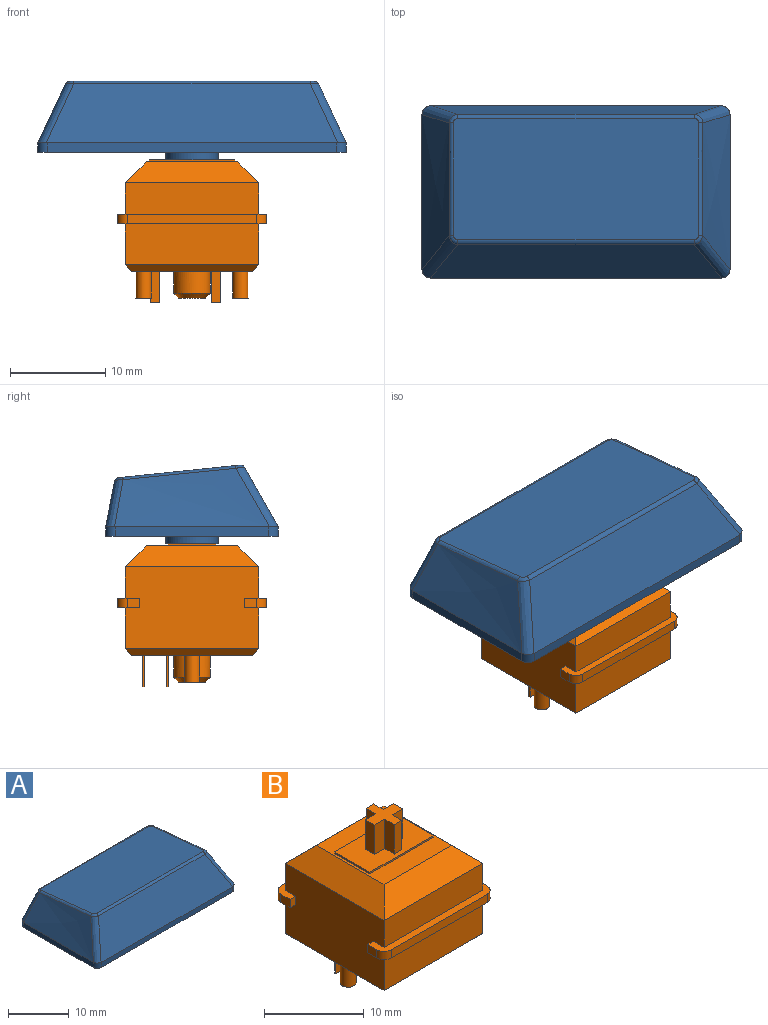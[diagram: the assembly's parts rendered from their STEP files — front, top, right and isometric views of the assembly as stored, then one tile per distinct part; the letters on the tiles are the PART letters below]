
ASSEMBLY  parts=2 mates=1
PART A: 50 faces, bbox 35.5x21.6x10.6 mm
  f0: plane 32.35x18.1mm, normal (0,0,-1), area 96mm2, adj f1,f2,f3,f4,f10,f12,f14,f16
  f1: plane 30.35x1mm, normal (0,-1,0), area 30.3mm2, adj f0,f8,f10,f12
  f2: plane 16.1x1mm, normal (1,0,0), area 16.1mm2, adj f0,f9,f10,f16
  f3: plane 30.35x1mm, normal (0,1,0), area 30.3mm2, adj f0,f6,f14,f15,f16,f17
  f4: plane 16.1x1mm, normal (-1,0,0), area 16.1mm2, adj f0,f7,f12,f14
  f5: plane 25.78x12.74mm, normal (0,0.1,0.99), area 329.4mm2, adj f18,f19,f20,f21,f22,f23,f24,f25
  f6: plane 30.26x4.75mm, normal (0,0.98,0.19), area 133.2mm2, adj f3,f15,f17,f20
  f7: bspline ~18.1x6.51mm, area 88.3mm2, adj f4,f12,f13,f14,f15,f19
  f8: plane 30.6x6.23mm, normal (0,-0.87,0.49), area 198.3mm2, adj f1,f10,f11,f12,f13,f23
  f9: bspline ~18.1x6.51mm, area 88.3mm2, adj f2,f10,f11,f16,f17,f24
  f10: cylinder r=1mm len=1.08mm, axis (0,0,1), area 1.7mm2, adj f0,f1,f2,f8,f9,f11
  f11: bspline ~8x5.25mm, area 10.6mm2, adj f8,f9,f10,f25
  f12: cylinder r=1mm len=1.08mm, axis (0,0,-1), area 1.7mm2, adj f0,f1,f4,f7,f8,f13
  f13: bspline ~8.02x5.26mm, area 10.6mm2, adj f7,f8,f12,f21
  f14: cylinder r=1mm len=1.01mm, axis (0,0,1), area 1.6mm2, adj f0,f3,f4,f7,f15
  f15: bspline ~7.53x4.96mm, area 8.3mm2, adj f3,f6,f7,f14,f18
  f16: cylinder r=1mm len=1.01mm, axis (0,0,-1), area 1.6mm2, adj f0,f2,f3,f9,f17
  f17: bspline ~7.51x4.95mm, area 8.3mm2, adj f3,f6,f9,f16,f22
  f18: bspline ~1.23x0.97mm, area 0.6mm2, adj f5,f15,f19,f20
  f19: bspline ~17.25x2.02mm, area 6.5mm2, adj f5,f7,f18,f21
  f20: cylinder r=0.5mm len=24.79mm, axis (-1,0,0), area 15.8mm2, adj f5,f6,f18,f22
  f21: bspline ~1.16x0.98mm, area 0.6mm2, adj f5,f13,f19,f23
  f22: bspline ~1.23x1.14mm, area 0.6mm2, adj f5,f17,f20,f24
  f23: cylinder r=0.5mm len=24.78mm, axis (-1,0,0), area 14.4mm2, adj f5,f8,f21,f25
  f24: bspline ~17.24x2.02mm, area 6.5mm2, adj f5,f9,f22,f25
  f25: bspline ~1.16x1mm, area 0.6mm2, adj f5,f11,f23,f24
  f26: plane 30.35x0.74mm, normal (0,1,0), area 22.3mm2, adj f0,f27,f29,f33
  f27: plane 16.13x0.81mm, normal (-1,0,0), area 12.2mm2, adj f0,f26,f28,f33,f34
  f28: plane 30.35x0.91mm, normal (0,-1,0), area 27.5mm2, adj f0,f27,f29,f31,f32,f34
  f29: plane 16.13x0.81mm, normal (1,0,0), area 12.2mm2, adj f0,f26,f28,f32,f33
  f30: plane 26.35x13.18mm, normal (0,-0.1,-0.99), area 280.3mm2, adj f31,f32,f33,f34,f45
  f31: plane 30.17x4.31mm, normal (0,-0.98,-0.19), area 121mm2, adj f28,f30,f32,f34
  f32: offset ~20.1x8.51mm, area 80.9mm2, adj f28,f29,f30,f31,f33
  f33: plane 30.38x5.75mm, normal (0,0.87,-0.49), area 182.1mm2, adj f26,f27,f29,f30,f32,f34
  f34: offset ~20.1x8.51mm, area 80.9mm2, adj f27,f28,f30,f31,f33
  f35: plane 6.68x1.35mm, normal (-1,0,0), area 8.9mm2, adj f36,f44,f47,f49
  f36: plane 6.68x1.5mm, normal (0,-1,0), area 10mm2, adj f35,f37,f44,f49
  f37: plane 6.82x1.3mm, normal (-1,0,0), area 8.8mm2, adj f36,f38,f44,f49
  f38: plane 6.82x1.5mm, normal (0,1,0), area 10.2mm2, adj f37,f39,f44,f49
  f39: plane 6.96x1.35mm, normal (-1,0,0), area 9.3mm2, adj f38,f40,f44,f49
  f40: plane 6.96x1mm, normal (0,1,0), area 7mm2, adj f39,f41,f44,f49
  f41: plane 6.96x1.35mm, normal (1,0,0), area 9.3mm2, adj f40,f42,f44,f49
  f42: plane 6.82x1.5mm, normal (0,1,0), area 10.2mm2, adj f41,f43,f44,f49
  f43: plane 6.82x1.3mm, normal (1,0,0), area 8.8mm2, adj f42,f44,f46,f49
  f44: plane 5.5x5.5mm, normal (0,0,-1), area 15.9mm2, adj f35,f36,f37,f38,f39,f40,f41,f42
  f45: cylinder r=2.75mm len=6.47mm, axis (0,0,-1), area 111.7mm2, adj f30,f44
  f46: plane 6.68x1.5mm, normal (0,-1,0), area 10mm2, adj f43,f44,f48,f49
  f47: plane 6.54x1mm, normal (0,-1,0), area 6.5mm2, adj f35,f44,f48,f49
  f48: plane 6.68x1.35mm, normal (1,0,0), area 8.9mm2, adj f44,f46,f47,f49
  f49: plane 4x4mm, normal (0,-0.1,-0.99), area 7.9mm2, adj f35,f36,f37,f38,f39,f40,f41,f42
PART B: 69 faces, bbox 15.6x15.6x18.6 mm
  f0: plane 15.6x2.3mm, normal (0,0,-1), area 14.4mm2, adj f2,f3,f28,f30,f35,f60,f62,f63
  f1: plane 15.6x2.3mm, normal (0,0,-1), area 14.4mm2, adj f28,f30,f33,f34,f36,f59,f61,f64
  f2: plane 1.3x1mm, normal (1,0,0), area 1.3mm2, adj f0,f32,f62,f66
  f3: plane 1.3x1mm, normal (-1,0,0), area 1.3mm2, adj f0,f32,f63,f68
  f4: plane 15.6x2.3mm, normal (0,0,1), area 14.4mm2, adj f28,f30,f31,f33,f34,f36,f61,f64
  f5: plane 14x2.2mm, normal (-0.71,0,0.71), area 36.7mm2, adj f6,f7,f26,f30
  f6: plane 14x2.2mm, normal (0,-0.71,0.71), area 36.7mm2, adj f5,f7,f27,f31
  f7: plane 9.6x9.6mm, normal (0,0,1), area 47.2mm2, adj f5,f6,f8,f9,f10,f11,f26,f27
  f8: plane 5x0.2mm, normal (1,0,0), area 1mm2, adj f7,f9,f11,f12
  f9: plane 9x0.2mm, normal (0,1,0), area 1.8mm2, adj f7,f8,f10,f12
  f10: plane 5x0.2mm, normal (-1,0,0), area 1mm2, adj f7,f9,f11,f12
  f11: plane 9x0.2mm, normal (0,-1,0), area 1.8mm2, adj f7,f8,f10,f12
  f12: plane 9x5mm, normal (0,0,1), area 36.9mm2, adj f8,f9,f10,f11,f13,f14,f15,f16
  f13: plane 3.6x1.35mm, normal (1,0,0), area 4.9mm2, adj f12,f14,f24,f25
  f14: plane 3.6x1.08mm, normal (0,1,0), area 3.9mm2, adj f12,f13,f15,f25
  f15: plane 3.6x1.35mm, normal (-1,0,0), area 4.9mm2, adj f12,f14,f16,f25
  f16: plane 3.6x1.46mm, normal (0,1,0), area 5.3mm2, adj f12,f15,f17,f25
  f17: plane 3.6x1.3mm, normal (-1,0,0), area 4.7mm2, adj f12,f16,f18,f25
  f18: plane 3.6x1.46mm, normal (0,-1,0), area 5.3mm2, adj f12,f17,f19,f25
  f19: plane 3.6x1.35mm, normal (-1,0,0), area 4.9mm2, adj f12,f18,f20,f25
  f20: plane 3.6x1.08mm, normal (0,-1,0), area 3.9mm2, adj f12,f19,f21,f25
  f21: plane 3.6x1.35mm, normal (1,0,0), area 4.9mm2, adj f12,f20,f22,f25
  f22: plane 3.6x1.46mm, normal (0,-1,0), area 5.3mm2, adj f12,f21,f23,f25
  f23: plane 3.6x1.3mm, normal (1,0,0), area 4.7mm2, adj f12,f22,f24,f25
  f24: plane 3.6x1.46mm, normal (0,1,0), area 5.3mm2, adj f12,f13,f23,f25
  f25: plane 4x4mm, normal (0,0,1), area 8.1mm2, adj f13,f14,f15,f16,f17,f18,f19,f20
  f26: plane 14x2.2mm, normal (0,0.71,0.71), area 36.7mm2, adj f5,f7,f27,f29
  f27: plane 14x2.2mm, normal (0.71,0,0.71), area 36.7mm2, adj f6,f7,f26,f28
  f28: plane 14x8.6mm, normal (1,0,0), area 117.4mm2, adj f0,f1,f4,f27,f29,f31,f32,f55
  f29: plane 14x3.3mm, normal (0,1,0), area 46.2mm2, adj f26,f28,f30,f32
  f30: plane 14x8.6mm, normal (-1,0,0), area 117.4mm2, adj f0,f1,f4,f5,f29,f31,f32,f57
  f31: plane 14x3.3mm, normal (0,-1,0), area 46.2mm2, adj f4,f6,f28,f30
  f32: plane 15.6x2.3mm, normal (0,0,1), area 14.4mm2, adj f2,f3,f28,f29,f30,f35,f62,f63
  f33: plane 13.6x1mm, normal (0,-1,0), area 13.6mm2, adj f1,f4,f61,f64
  f34: plane 1.3x1mm, normal (1,0,0), area 1.3mm2, adj f1,f4,f61,f65
  f35: plane 13.6x1mm, normal (0,1,0), area 13.6mm2, adj f0,f32,f62,f63
  f36: plane 1.3x1mm, normal (-1,0,0), area 1.3mm2, adj f1,f4,f64,f67
  f37: plane 2.85x2.85mm, normal (0,0,-1), area 6.4mm2, adj f38
  f38: cone r=1.43mm half-angle=45deg, axis (0,0,1), area 7.4mm2, adj f37,f43
  f39: plane 1x0.2mm, normal (0,0,-1), area 0.2mm2, adj f44,f45,f46,f47
  f40: plane 1x0.2mm, normal (0,0,-1), area 0.2mm2, adj f48,f49,f50,f51
  f41: plane 1.6x1.6mm, normal (0,0,-1), area 2mm2, adj f52
  f42: plane 1.6x1.6mm, normal (0,0,-1), area 2mm2, adj f53
  f43: cylinder r=1.93mm len=3.85mm, axis (0,0,1), area 27.8mm2, adj f38,f54
  f44: plane 3.3x0.2mm, normal (-1,0,0), area 0.7mm2, adj f39,f45,f47,f54
  f45: plane 3.3x1mm, normal (0,1,0), area 3.3mm2, adj f39,f44,f46,f54
  f46: plane 3.3x0.2mm, normal (1,0,0), area 0.7mm2, adj f39,f45,f47,f54
  f47: plane 3.3x1mm, normal (0,-1,0), area 3.3mm2, adj f39,f44,f46,f54
  f48: plane 3.3x0.2mm, normal (-1,0,0), area 0.7mm2, adj f40,f49,f51,f54
  f49: plane 3.3x1mm, normal (0,1,0), area 3.3mm2, adj f40,f48,f50,f54
  f50: plane 3.3x0.2mm, normal (1,0,0), area 0.7mm2, adj f40,f49,f51,f54
  f51: plane 3.3x1mm, normal (0,-1,0), area 3.3mm2, adj f40,f48,f50,f54
  f52: cylinder r=0.8mm len=2.8mm, axis (0,0,1), area 14.1mm2, adj f41,f54
  f53: cylinder r=0.8mm len=2.8mm, axis (0,0,1), area 14.1mm2, adj f42,f54
  f54: plane 12.6x12.6mm, normal (0,0,-1), area 142.7mm2, adj f43,f44,f45,f46,f47,f48,f49,f50
  f55: plane 14x0.7mm, normal (0.71,0,-0.71), area 13.2mm2, adj f28,f54,f56,f58
  f56: plane 14x0.7mm, normal (0,0.71,-0.71), area 13.2mm2, adj f54,f55,f57,f60
  f57: plane 14x0.7mm, normal (-0.71,0,-0.71), area 13.2mm2, adj f30,f54,f56,f58
  f58: plane 14x0.7mm, normal (0,-0.71,-0.71), area 13.2mm2, adj f54,f55,f57,f59
  f59: plane 14x4.3mm, normal (0,-1,0), area 60.2mm2, adj f1,f28,f30,f58
  f60: plane 14x4.3mm, normal (0,1,0), area 60.2mm2, adj f0,f28,f30,f56
  f61: cylinder r=1mm len=1mm, axis (0,0,-1), area 1.6mm2, adj f1,f4,f33,f34
  f62: cylinder r=1mm len=1mm, axis (0,0,1), area 1.6mm2, adj f0,f2,f32,f35
  f63: cylinder r=1mm len=1mm, axis (0,0,-1), area 1.6mm2, adj f0,f3,f32,f35
  f64: cylinder r=1mm len=1mm, axis (0,0,1), area 1.6mm2, adj f1,f4,f33,f36
  f65: plane 1x0.8mm, normal (0,1,0), area 0.8mm2, adj f1,f4,f28,f34
  f66: plane 1x0.8mm, normal (0,-1,0), area 0.8mm2, adj f0,f2,f28,f32
  f67: plane 1x0.8mm, normal (0,1,0), area 0.8mm2, adj f1,f4,f30,f36
  f68: plane 1x0.8mm, normal (0,-1,0), area 0.8mm2, adj f0,f3,f30,f32
PLACE A t=(0,0,11.7)mm
PLACE B at identity fixed
MATE fastened A.f45 <-> B.f38  axis (0,0,-1) through (0,0,11.7)mm
